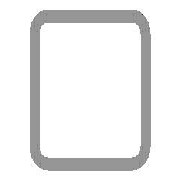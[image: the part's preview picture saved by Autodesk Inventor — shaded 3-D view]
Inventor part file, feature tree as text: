
AUTODESK INVENTOR PART (.ipt)
format: ipt  version: 2025.1 (Build 291241020, 241B)  size: 134,144 bytes
history: native  units: mm (DEFAULTED — no unit token found)
features: other x4, sketch x1, plane x1
ambient origin geometry x8: Origin, YZ Plane, XZ Plane, XY Plane, X Axis, Y Axis, Z Axis, Center Point
bodies: Solid1 (feature_tree), Body (feature_tree)
feature tree (6):
  parser-record x1  (decoder bookkeeping rows leaked as tree rows — omitted from the tree; the rows remain in map.json)
  other  "Driven Length"
  other  "Start Plane"
  other  "End Plane"
  sketch  "Sketch3"  dims[d3=2400.0mm d4=0.0mm d7=6.0mm d9=100.0mm d11=100.0mm d12=3.0mm d13=-0.0mm d14=2400.0mm d15=50.0mm d16=50.0mm d17=90.0deg d18=2400.0mm]
  plane  "Work Plane3"
